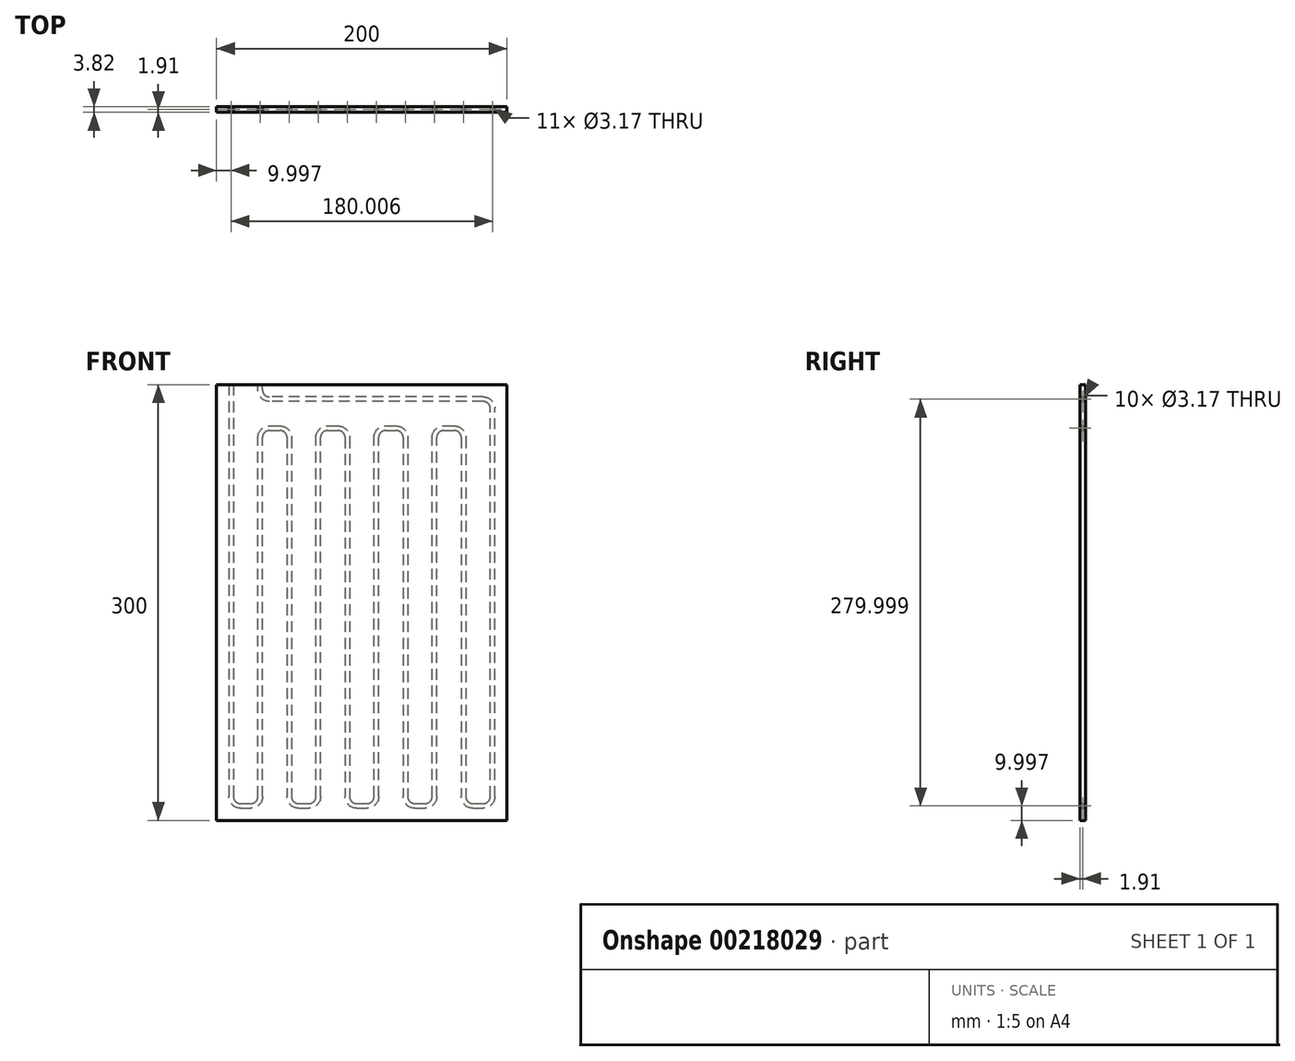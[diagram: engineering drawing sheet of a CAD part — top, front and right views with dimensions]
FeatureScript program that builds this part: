
annotation { "Feature Type Name" : "Feature", "Feature Type Description" : "" }
export const myFeature = defineFeature(function(context is Context, id is Id, definition is map)
    precondition{}
    {
        {
            var Q0;
            Q0=qCreatedBy(makeId("Front.planeOp"),FACE);
            var sketch = newSketch(context, id + "F0", { "sketchPlane" : qUnion([Q0])});
            skLineSegment(sketch, "E0.bottom", {"start": v(100, 150) * mm, "end": v(-100, 150) * mm});
            skLineSegment(sketch, "E0.top", {"start": v(100, -150) * mm, "end": v(-100, -150) * mm});
            skLineSegment(sketch, "E0.left", {"start": v(100, 150) * mm, "end": v(100, -150) * mm});
            skLineSegment(sketch, "E0.right", {"start": v(-100, 150) * mm, "end": v(-100, -150) * mm});
            skPoint(sketch, "E0.middle", {"position": v(0, 0) * mm});
            skSolve(sketch);
        }
        {
            var Q0;
            Q0=makeQuery(id+"F0.imprint","IMPRINT",FACE,{"disambiguationData":[TD([[makeQuery(id+"F0.imprint","IMPRINT",EDGE,{"derivedFrom":sQuery(id+"F0.wireOp",EDGE,"E0.bottom")}),1.0]])]});
            var sketch = newSketch(context, id + "F1", { "sketchPlane" : qUnion([Q0])});
            skLineSegment(sketch, "E1", {"start": v(-90, 159.9) * mm, "end": v(-90, -133.65) * mm});
            skLineSegment(sketch, "E2", {"start": v(-83.65, -140) * mm, "end": v(-76.35, -140) * mm});
            skLineSegment(sketch, "E3", {"start": v(-70, -133.65) * mm, "end": v(-70, 113.65) * mm});
            skLineSegment(sketch, "E4", {"start": v(-63.65, 120) * mm, "end": v(-56.35, 120) * mm});
            skLineSegment(sketch, "E5", {"start": v(-50, 113.65) * mm, "end": v(-50, -133.65) * mm});
            skLineSegment(sketch, "E6", {"start": v(-43.65, -140) * mm, "end": v(-36.35, -140) * mm});
            skLineSegment(sketch, "E7", {"start": v(-30, -133.65) * mm, "end": v(-30, 113.65) * mm});
            skLineSegment(sketch, "E8", {"start": v(-23.65, 120) * mm, "end": v(-16.35, 120) * mm});
            skLineSegment(sketch, "E9", {"start": v(-10, 113.65) * mm, "end": v(-10, -133.65) * mm});
            skLineSegment(sketch, "E10", {"start": v(-3.65, -140) * mm, "end": v(3.65, -140) * mm});
            skLineSegment(sketch, "E11", {"start": v(10, -133.65) * mm, "end": v(10, 113.65) * mm});
            skLineSegment(sketch, "E12", {"start": v(16.35, 120) * mm, "end": v(23.65, 120) * mm});
            skLineSegment(sketch, "E13", {"start": v(30, 113.65) * mm, "end": v(30, -133.65) * mm});
            skLineSegment(sketch, "E14", {"start": v(36.35, -140) * mm, "end": v(43.65, -140) * mm});
            skLineSegment(sketch, "E15", {"start": v(50, -133.65) * mm, "end": v(50, 113.65) * mm});
            skLineSegment(sketch, "E16", {"start": v(56.35, 120) * mm, "end": v(63.65, 120) * mm});
            skLineSegment(sketch, "E17", {"start": v(70, 113.65) * mm, "end": v(70, -133.65) * mm});
            skLineSegment(sketch, "E18", {"start": v(76.35, -140) * mm, "end": v(83.65, -140) * mm});
            skLineSegment(sketch, "E19", {"start": v(90, -133.65) * mm, "end": v(90, 133.64) * mm});
            skLineSegment(sketch, "E20", {"start": v(83.65, 140) * mm, "end": v(-63.65, 140) * mm});
            skLineSegment(sketch, "E21", {"start": v(-70, 146.34) * mm, "end": v(-70, 159.9) * mm});
            skPoint(sketch, "E22.visualSharp", {"position": v(-90, -140) * mm});
            skArc(sketch, "E22.filletArc", {"start": v(-90, -133.65) * mm, "mid": v(-88.14, -138.14) * mm, "end": v(-83.65, -140) * mm});
            skPoint(sketch, "E23.visualSharp", {"position": v(-70, -140) * mm});
            skArc(sketch, "E23.filletArc", {"start": v(-76.35, -140) * mm, "mid": v(-71.86, -138.14) * mm, "end": v(-70, -133.65) * mm});
            skPoint(sketch, "E24.visualSharp", {"position": v(-50, -140) * mm});
            skArc(sketch, "E24.filletArc", {"start": v(-50, -133.65) * mm, "mid": v(-48.14, -138.14) * mm, "end": v(-43.65, -140) * mm});
            skPoint(sketch, "E25.visualSharp", {"position": v(-30, -140) * mm});
            skArc(sketch, "E25.filletArc", {"start": v(-36.35, -140) * mm, "mid": v(-31.86, -138.14) * mm, "end": v(-30, -133.65) * mm});
            skPoint(sketch, "E26.visualSharp", {"position": v(-10, -140) * mm});
            skArc(sketch, "E26.filletArc", {"start": v(-10, -133.65) * mm, "mid": v(-8.14, -138.14) * mm, "end": v(-3.65, -140) * mm});
            skPoint(sketch, "E27.visualSharp", {"position": v(10, -140) * mm});
            skArc(sketch, "E27.filletArc", {"start": v(3.65, -140) * mm, "mid": v(8.14, -138.14) * mm, "end": v(10, -133.65) * mm});
            skPoint(sketch, "E28.visualSharp", {"position": v(30, -140) * mm});
            skArc(sketch, "E28.filletArc", {"start": v(30, -133.65) * mm, "mid": v(31.86, -138.14) * mm, "end": v(36.35, -140) * mm});
            skPoint(sketch, "E29.visualSharp", {"position": v(50, -140) * mm});
            skArc(sketch, "E29.filletArc", {"start": v(43.65, -140) * mm, "mid": v(48.14, -138.14) * mm, "end": v(50, -133.65) * mm});
            skPoint(sketch, "E30.visualSharp", {"position": v(70, -140) * mm});
            skArc(sketch, "E30.filletArc", {"start": v(70, -133.65) * mm, "mid": v(71.86, -138.14) * mm, "end": v(76.35, -140) * mm});
            skPoint(sketch, "E31.visualSharp", {"position": v(90, -140) * mm});
            skArc(sketch, "E31.filletArc", {"start": v(83.65, -140) * mm, "mid": v(88.14, -138.14) * mm, "end": v(90, -133.65) * mm});
            skPoint(sketch, "E32.visualSharp", {"position": v(-70, 120) * mm});
            skArc(sketch, "E32.filletArc", {"start": v(-63.65, 120) * mm, "mid": v(-68.14, 118.14) * mm, "end": v(-70, 113.65) * mm});
            skPoint(sketch, "E33.visualSharp", {"position": v(-50, 120) * mm});
            skArc(sketch, "E33.filletArc", {"start": v(-50, 113.65) * mm, "mid": v(-51.86, 118.14) * mm, "end": v(-56.35, 120) * mm});
            skPoint(sketch, "E34.visualSharp", {"position": v(-30, 120) * mm});
            skArc(sketch, "E34.filletArc", {"start": v(-23.65, 120) * mm, "mid": v(-28.14, 118.14) * mm, "end": v(-30, 113.65) * mm});
            skPoint(sketch, "E35.visualSharp", {"position": v(-10, 120) * mm});
            skArc(sketch, "E35.filletArc", {"start": v(-10, 113.65) * mm, "mid": v(-11.86, 118.14) * mm, "end": v(-16.35, 120) * mm});
            skPoint(sketch, "E36.visualSharp", {"position": v(10, 120) * mm});
            skArc(sketch, "E36.filletArc", {"start": v(16.35, 120) * mm, "mid": v(11.86, 118.14) * mm, "end": v(10, 113.65) * mm});
            skPoint(sketch, "E37.visualSharp", {"position": v(30, 120) * mm});
            skArc(sketch, "E37.filletArc", {"start": v(30, 113.65) * mm, "mid": v(28.14, 118.14) * mm, "end": v(23.65, 120) * mm});
            skPoint(sketch, "E38.visualSharp", {"position": v(50, 120) * mm});
            skArc(sketch, "E38.filletArc", {"start": v(56.35, 120) * mm, "mid": v(51.86, 118.14) * mm, "end": v(50, 113.65) * mm});
            skPoint(sketch, "E39.visualSharp", {"position": v(70, 120) * mm});
            skArc(sketch, "E39.filletArc", {"start": v(70, 113.65) * mm, "mid": v(68.14, 118.14) * mm, "end": v(63.65, 120) * mm});
            skPoint(sketch, "E40.visualSharp", {"position": v(90, 140) * mm});
            skArc(sketch, "E40.filletArc", {"start": v(90, 133.64) * mm, "mid": v(88.14, 138.13) * mm, "end": v(83.65, 140) * mm});
            skPoint(sketch, "E41.visualSharp", {"position": v(-70, 140) * mm});
            skArc(sketch, "E41.filletArc", {"start": v(-70, 146.34) * mm, "mid": v(-68.14, 141.85) * mm, "end": v(-63.65, 140) * mm});
            skSolve(sketch);
        }
        {
            var Q0;
            Q0=makeQuery(id+"F0.imprint","IMPRINT",FACE,{"disambiguationData":[TD([[makeQuery(id+"F0.imprint","IMPRINT",EDGE,{"derivedFrom":sQuery(id+"F0.wireOp",EDGE,"E0.bottom")}),1.0]])]});
            extrude(context, id + "F2", {"entities" : qUnion([Q0]), "depth" : 3.8 * mm, "symmetric" : true});
        }
        {
            var Q0;
            Q0=sQuery(id+"F1.wireOp",VERTEX,"E21.end");
            var Q1;
            Q1=qCreatedBy(makeId("Top.planeOp"),FACE);
            cPlane(context, id + "F3", {"entities" : qUnion([Q0, Q1]), "cplaneType" : CPlaneType.PLANE_POINT, "offset" : 25.4 * mm, "width" : 152.4 * mm, "height" : 152.4 * mm});
        }
        {
            var Q0;
            Q0=qCreatedBy(id+"F3.planeOp",FACE);
            var sketch = newSketch(context, id + "F4", { "sketchPlane" : qUnion([Q0])});
            skCircle(sketch, "E42", {"center": v(-70.02, 0) * mm, "radius": 1.59 * mm});
            skCircle(sketch, "E43", {"center": v(-90, 0) * mm, "radius": 1.59 * mm});
            skSolve(sketch);
        }
        {
            var Q0;
            Q0=makeQuery(id+"F4.imprint","IMPRINT",FACE,{"disambiguationData":[TD([[makeQuery(id+"F4.imprint","IMPRINT",EDGE,{"derivedFrom":sQuery(id+"F4.wireOp",EDGE,"E43")}),1.0]])]});
            var Q1;
            Q1=sQuery(id+"F1.wireOp",EDGE,"E1");
            var Q2;
            Q2=sQuery(id+"F1.wireOp",EDGE,"E22.filletArc");
            var Q3;
            Q3=sQuery(id+"F1.wireOp",EDGE,"E2");
            var Q4;
            Q4=sQuery(id+"F1.wireOp",EDGE,"E23.filletArc");
            var Q5;
            Q5=sQuery(id+"F1.wireOp",EDGE,"E3");
            var Q6;
            Q6=sQuery(id+"F1.wireOp",EDGE,"E32.filletArc");
            var Q7;
            Q7=sQuery(id+"F1.wireOp",EDGE,"E4");
            var Q8;
            Q8=sQuery(id+"F1.wireOp",EDGE,"E33.filletArc");
            var Q9;
            Q9=sQuery(id+"F1.wireOp",EDGE,"E5");
            var Q10;
            Q10=sQuery(id+"F1.wireOp",EDGE,"E24.filletArc");
            var Q11;
            Q11=sQuery(id+"F1.wireOp",EDGE,"E6");
            var Q12;
            Q12=sQuery(id+"F1.wireOp",EDGE,"E25.filletArc");
            var Q13;
            Q13=sQuery(id+"F1.wireOp",EDGE,"E7");
            var Q14;
            Q14=sQuery(id+"F1.wireOp",EDGE,"E34.filletArc");
            var Q15;
            Q15=sQuery(id+"F1.wireOp",EDGE,"E8");
            var Q16;
            Q16=sQuery(id+"F1.wireOp",EDGE,"E35.filletArc");
            var Q17;
            Q17=sQuery(id+"F1.wireOp",EDGE,"E9");
            var Q18;
            Q18=sQuery(id+"F1.wireOp",EDGE,"E26.filletArc");
            var Q19;
            Q19=sQuery(id+"F1.wireOp",EDGE,"E10");
            var Q20;
            Q20=sQuery(id+"F1.wireOp",EDGE,"E27.filletArc");
            var Q21;
            Q21=sQuery(id+"F1.wireOp",EDGE,"E11");
            var Q22;
            Q22=sQuery(id+"F1.wireOp",EDGE,"E36.filletArc");
            var Q23;
            Q23=sQuery(id+"F1.wireOp",EDGE,"E12");
            var Q24;
            Q24=sQuery(id+"F1.wireOp",EDGE,"E37.filletArc");
            var Q25;
            Q25=sQuery(id+"F1.wireOp",EDGE,"E13");
            var Q26;
            Q26=sQuery(id+"F1.wireOp",EDGE,"E28.filletArc");
            var Q27;
            Q27=sQuery(id+"F1.wireOp",EDGE,"E14");
            var Q28;
            Q28=sQuery(id+"F1.wireOp",EDGE,"E29.filletArc");
            var Q29;
            Q29=sQuery(id+"F1.wireOp",EDGE,"E15");
            var Q30;
            Q30=sQuery(id+"F1.wireOp",EDGE,"E38.filletArc");
            var Q31;
            Q31=sQuery(id+"F1.wireOp",EDGE,"E16");
            var Q32;
            Q32=sQuery(id+"F1.wireOp",EDGE,"E39.filletArc");
            var Q33;
            Q33=sQuery(id+"F1.wireOp",EDGE,"E17");
            var Q34;
            Q34=sQuery(id+"F1.wireOp",EDGE,"E30.filletArc");
            var Q35;
            Q35=sQuery(id+"F1.wireOp",EDGE,"E18");
            var Q36;
            Q36=sQuery(id+"F1.wireOp",EDGE,"E31.filletArc");
            var Q37;
            Q37=sQuery(id+"F1.wireOp",EDGE,"E19");
            var Q38;
            Q38=sQuery(id+"F1.wireOp",EDGE,"E40.filletArc");
            var Q39;
            Q39=sQuery(id+"F1.wireOp",EDGE,"E20");
            var Q40;
            Q40=sQuery(id+"F1.wireOp",EDGE,"E41.filletArc");
            var Q41;
            Q41=sQuery(id+"F1.wireOp",EDGE,"E21");
            sweep(context, id + "F5", {"operationType" : NewBodyOperationType.REMOVE, "profiles" : qUnion([Q0]), "path" : qUnion([Q1, Q2, Q3, Q4, Q5, Q6, Q7, Q8, Q9, Q10, Q11, Q12, Q13, Q14, Q15, Q16, Q17, Q18, Q19, Q20, Q21, Q22, Q23, Q24, Q25, Q26, Q27, Q28, Q29, Q30, Q31, Q32, Q33, Q34, Q35, Q36, Q37, Q38, Q39, Q40, Q41])});
        }
    });
